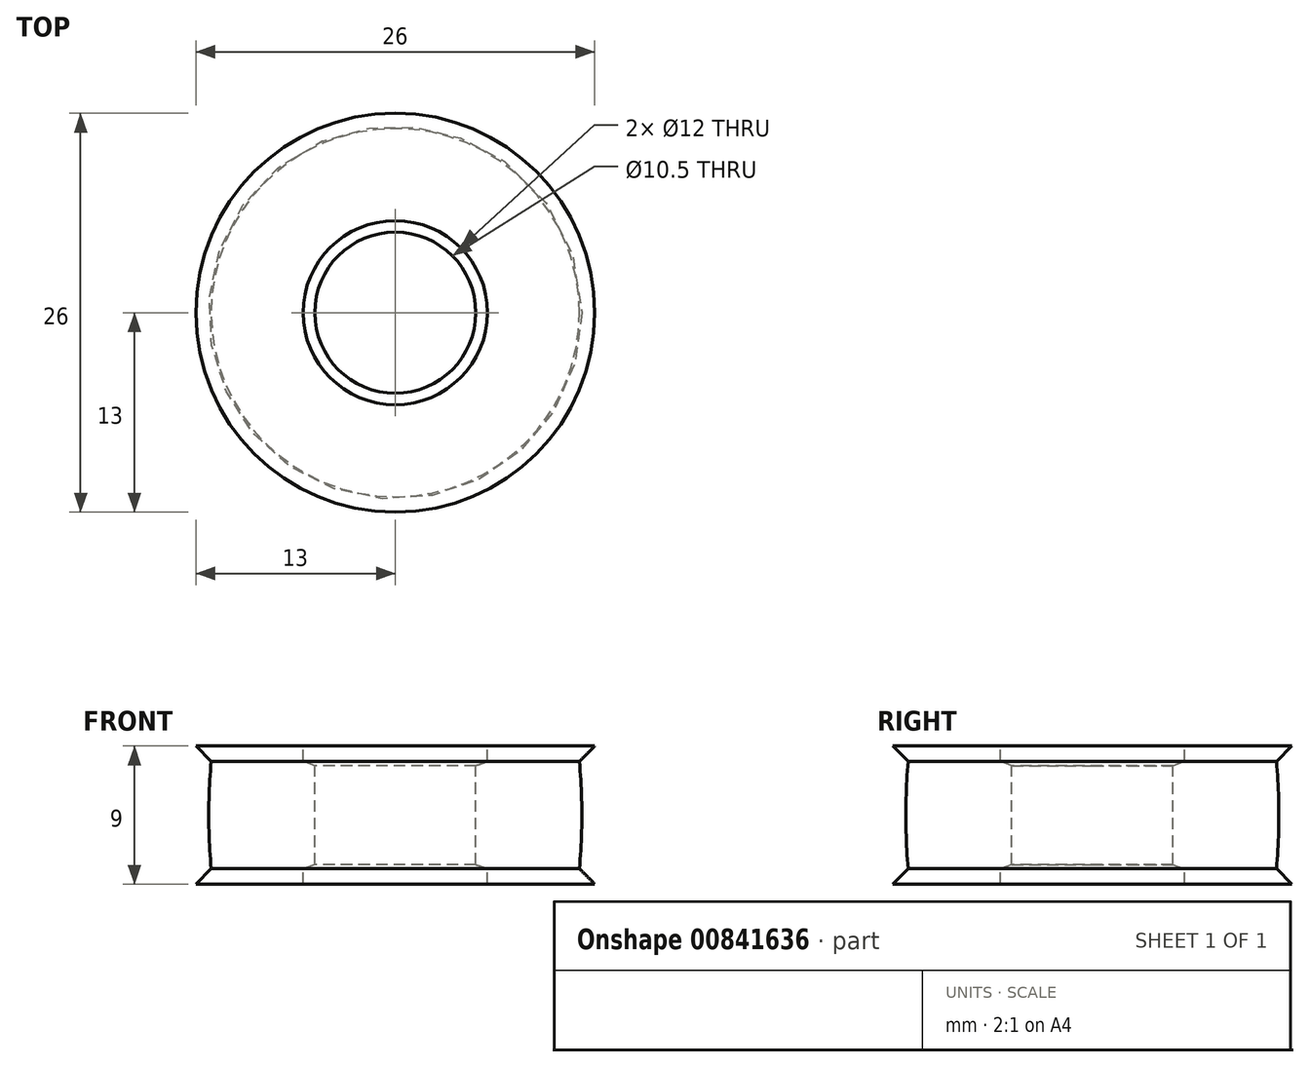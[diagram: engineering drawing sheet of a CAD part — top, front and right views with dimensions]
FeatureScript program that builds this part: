
annotation { "Feature Type Name" : "Feature", "Feature Type Description" : "" }
export const myFeature = defineFeature(function(context is Context, id is Id, definition is map)
    precondition{}
    {
        {
            var Q0;
            Q0=qCreatedBy(makeId("Front.planeOp"),FACE);
            var sketch = newSketch(context, id + "F0", { "sketchPlane" : qUnion([Q0])});
            skLineSegment(sketch, "E0", {"start": v(0, 0) * mm, "end": v(0, -9) * mm, "construction": true});
            skLineSegment(sketch, "E1", {"start": v(13, -9) * mm, "end": v(12, -8) * mm});
            skLineSegment(sketch, "E2", {"start": v(12, -8) * mm, "end": v(12, -1) * mm});
            skLineSegment(sketch, "E3", {"start": v(12, -1) * mm, "end": v(13, 0) * mm});
            skArc(sketch, "E4", {"start": v(12, -8) * mm, "mid": v(12.15, -4.5) * mm, "end": v(12, -1) * mm});
            skLineSegment(sketch, "E5", {"start": v(5.25, -1.27) * mm, "end": v(5.25, -7.73) * mm});
            skLineSegment(sketch, "E6", {"start": v(6, -8) * mm, "end": v(6, -9) * mm});
            skLineSegment(sketch, "E7", {"start": v(6, 0) * mm, "end": v(6, -1) * mm});
            skLineSegment(sketch, "E8", {"start": v(6, -1) * mm, "end": v(5.25, -1.27) * mm});
            skLineSegment(sketch, "E9", {"start": v(5.25, -7.73) * mm, "end": v(6, -8) * mm});
            skLineSegment(sketch, "E10", {"start": v(6, 0) * mm, "end": v(13, 0) * mm});
            skLineSegment(sketch, "E11", {"start": v(13, -9) * mm, "end": v(6, -9) * mm});
            skSolve(sketch);
        }
        {
            var Q0;
            Q0 = qSketchRegion(id + "F0", true);
            var Q1;
            Q1 = qSketchRegion(id + "FuJ5QW741CVV3LI_1", true);
            var Q2;
            Q2=sQuery(id+"F0.wireOp",EDGE,"E0");
            revolve(context, id + "F1", {"surfaceOperationType" : NewSurfaceOperationType.NEW, "entities" : qUnion([Q0, Q1]), "axis" : qUnion([Q2]), "revolveType" : RevolveType.FULL});
        }
    });
